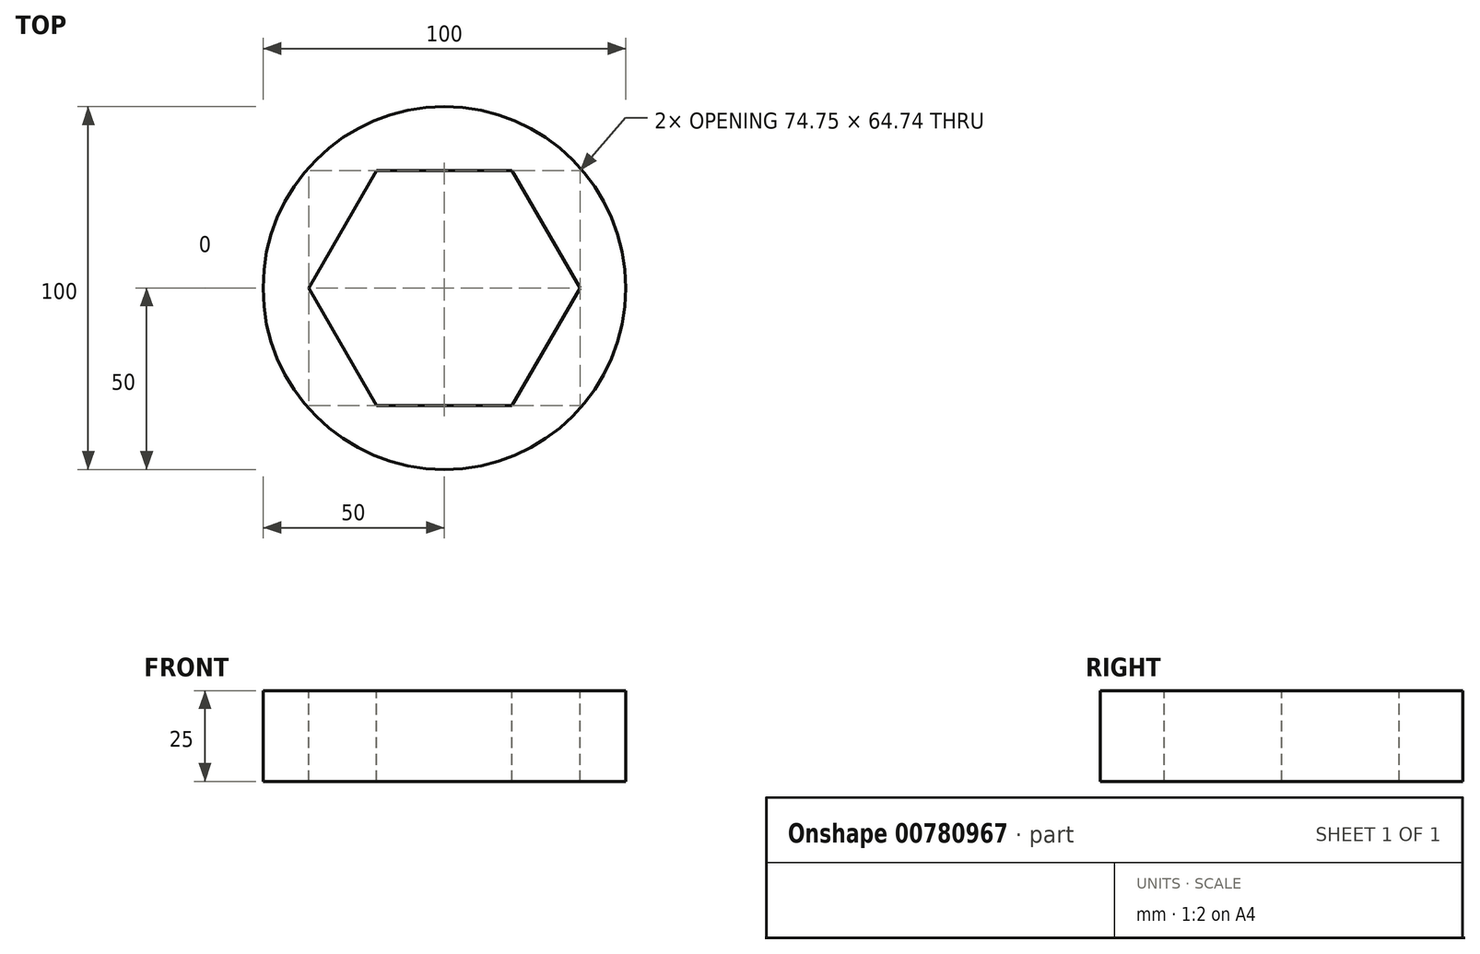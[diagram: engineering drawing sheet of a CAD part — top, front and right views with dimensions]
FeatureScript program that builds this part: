
annotation { "Feature Type Name" : "Feature", "Feature Type Description" : "" }
export const myFeature = defineFeature(function(context is Context, id is Id, definition is map)
    precondition{}
    {
        {
            var Q0;
            Q0=qCreatedBy(makeId("Top.planeOp"),FACE);
            var sketch = newSketch(context, id + "F0", { "sketchPlane" : qUnion([Q0])});
            skCircle(sketch, "E0", {"center": v(0, 0) * mm, "radius": 50 * mm});
            skSolve(sketch);
        }
        {
            var Q0;
            Q0 = qSketchRegion(id + "F0", true);
            extrude(context, id + "F1", {"entities" : qUnion([Q0]), "depth" : 25 * mm, "offsetDistance" : 25 * mm});
        }
        {
            var Q0;
            Q0=makeQuery(id+"F1.opExtrude","CAP_FACE",FACE,{"disambiguationData":[OSD([sQuery(id+"F0.wireOp",EDGE,"E0")])],"isStart":false});
            var sketch = newSketch(context, id + "F2", { "sketchPlane" : qUnion([Q0])});
            skCircle(sketch, "E1.cCircle", {"center": v(0, 0) * mm, "radius": 37.38 * mm, "construction": true});
            skLineSegment(sketch, "E1.0", {"start": v(37.38, 0) * mm, "end": v(18.69, -32.37) * mm});
            skLineSegment(sketch, "E1.1", {"start": v(18.69, -32.37) * mm, "end": v(-18.69, -32.37) * mm});
            skLineSegment(sketch, "E1.2", {"start": v(-18.69, -32.37) * mm, "end": v(-37.38, 0) * mm});
            skLineSegment(sketch, "E1.3", {"start": v(-37.38, 0) * mm, "end": v(-18.69, 32.37) * mm});
            skLineSegment(sketch, "E1.4", {"start": v(-18.69, 32.37) * mm, "end": v(18.69, 32.37) * mm});
            skLineSegment(sketch, "E1.5", {"start": v(18.69, 32.37) * mm, "end": v(37.38, 0) * mm});
            skSolve(sketch);
        }
        {
            var Q0;
            Q0 = qSketchRegion(id + "F2", true);
            extrude(context, id + "F3", {"entities" : qUnion([Q0]), "operationType" : NewBodyOperationType.REMOVE, "endBound" : BoundingType.THROUGH_ALL, "oppositeDirection" : true, "depth" : 25 * mm, "offsetDistance" : 25 * mm});
        }
    });
